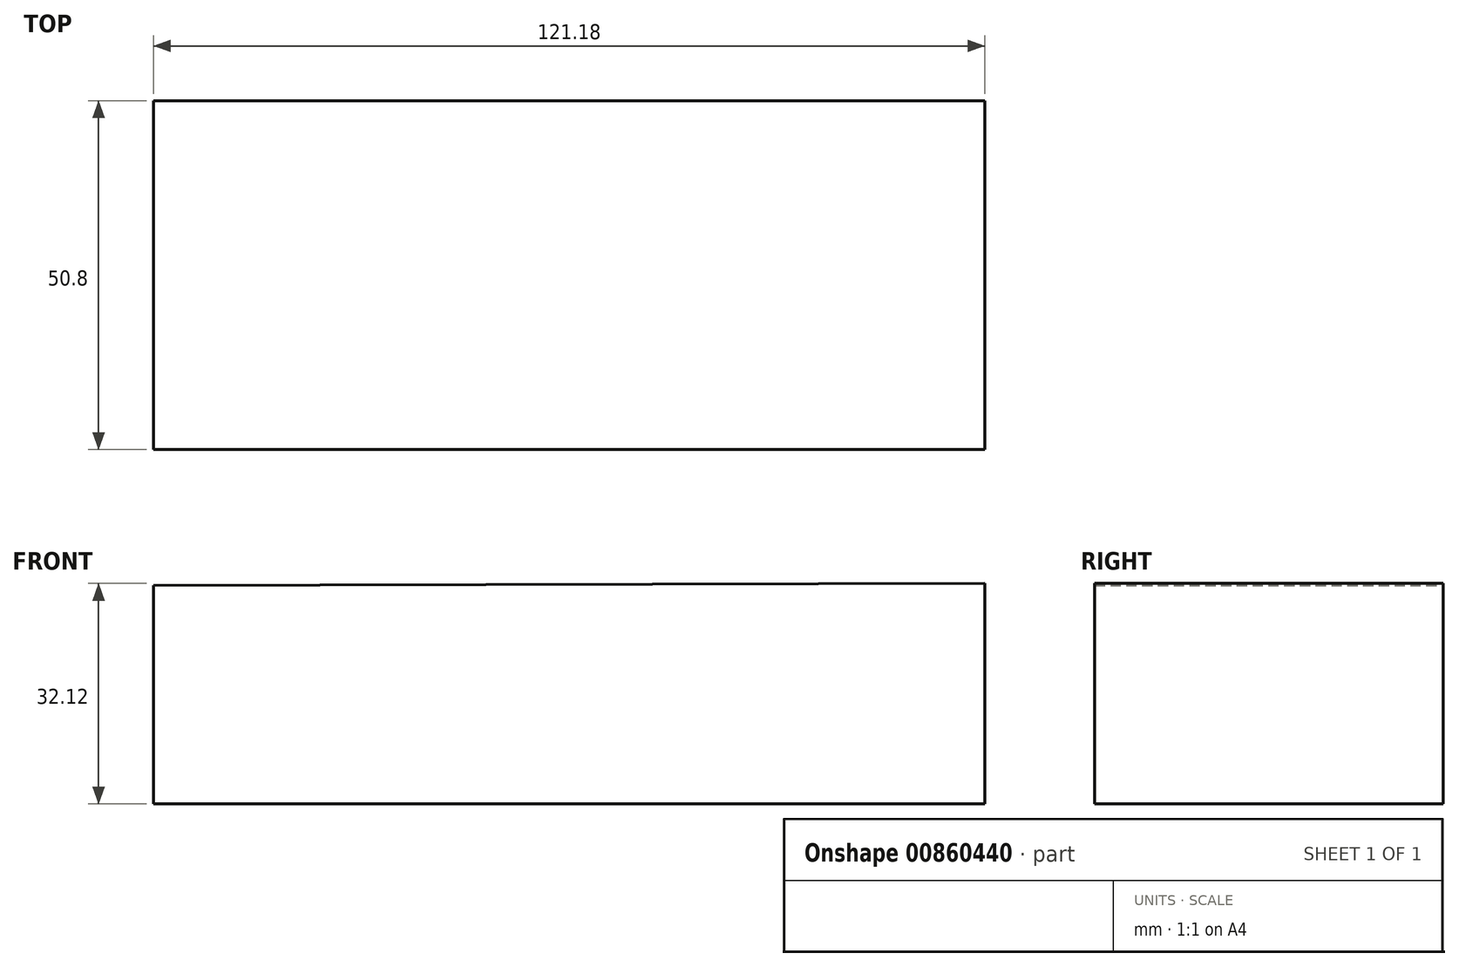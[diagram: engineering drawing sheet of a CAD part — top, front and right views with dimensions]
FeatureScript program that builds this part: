
annotation { "Feature Type Name" : "Feature", "Feature Type Description" : "" }
export const myFeature = defineFeature(function(context is Context, id is Id, definition is map)
    precondition{}
    {
        {
            var Q0;
            Q0=qCreatedBy(makeId("Front.planeOp"),FACE);
            var sketch = newSketch(context, id + "F0", { "sketchPlane" : qUnion([Q0])});
            skLineSegment(sketch, "E0", {"start": v(-60.6, 16.5) * mm, "end": v(-60.6, -15.33) * mm});
            skLineSegment(sketch, "E1", {"start": v(-60.6, -15.33) * mm, "end": v(60.6, -15.33) * mm});
            skLineSegment(sketch, "E2", {"start": v(60.6, -15.33) * mm, "end": v(60.6, 16.8) * mm});
            skLineSegment(sketch, "E3", {"start": v(60.6, 16.8) * mm, "end": v(-60.6, 16.5) * mm});
            skSolve(sketch);
        }
        {
            var Q0;
            Q0 = qSketchRegion(id + "F0", true);
            extrude(context, id + "F1", {"entities" : qUnion([Q0]), "depth" : 50.8 * mm, "offsetDistance" : 25.4 * mm});
        }
    });
